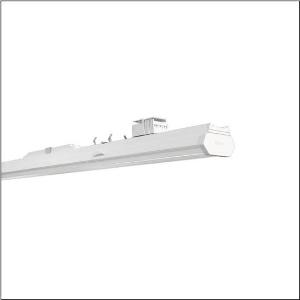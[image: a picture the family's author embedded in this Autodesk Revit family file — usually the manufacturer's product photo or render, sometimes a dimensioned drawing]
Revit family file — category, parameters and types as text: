
# Revit family: licross_r__21_protected_mo_52tp12dn4a5g_b875
name_source: partatom
category: Lighting Fixtures
units: mm (PartAtom-declared; Revit-internal decimal feet)

## family parameters
Cut with Voids When Loaded = No
Host = Face
Light Source = No
Part Type = Normal
Room Calculation Point = No
Round Connector Dimension = Use Diameter
Shared = No

## types (1)
- --- (1 x LED, 10700 lm, 62 W, 4000K)
    Apparent Load = 62 VA
    CIE Flux Codes = 73 92 98 99 100
    Color Rendering = 80
    Color Temperature = 4000K
    Default Elevation = 1800 mm
    Description = Licross® 21 Protected MO, luminaire insert, of sheet steel, galvanised, coil coated, white, length: 1.500mm, width: 90mm, height: 103mm, LED rated luminous flux: 10.700lm, light colour: 840, SDCM (Standard Deviation of Colour Matching)MacAdam ≤ 3 SDCM (initial), control gear: DALI 2, with plug, 5-pole, with phase selection, mains connection: 220..240V, AC, 50/60Hz, rated input power: 62W, internal wiring halogen-free, primary light control with lens, of plastic, primary optical cover: cover, of PMMA, light emission: direct distribution, primary light characteristic: symmetric, protection rating (complete): IP64, insulation class (complete): insulation class I (protective earthing), certification: CE, ENEC, VDE, UKCA, protection symbol: D if used in an environment with conductive dust loads with corresponding accessories, impact resistance: IK06, permissible ambient temperature for indoor applications: -25..+35°C, corresponds to IFS (International Featured Standards) requirements for safety and quality in the food industry, reducing of maximum allowable ambient temperature of 5°C with ceiling mounting, LABS conformity tested according to VDMA 24364:2018-05, packaging unit: 1 piece
    Height = 92 mm
    Lamp = 1 x LED
    Lamp Light Flux = 10700 lm
    Lamp Power = 62 W
    Lamp count = 1
    Length = 1500 mm
    Luminous efficacy = 173 lm/W
    Manufacturer = Siteco
    ModVariant = No
    Model = 52TP12DN4A5G
    Mounting Place = Ceiling
    Mounting Type = Pendant
    Number of Poles = 1
    OnlyDefault = Yes
    Power Factor = 1
    Product Name = Licross® 21 Protected MO
    Product group = luminaire insert | ceiling pendant
    ProductGroupID = 901
    Protection Class = Protection class I
    Protection Degree = IP 64
    RLX_Detail_Level = 1
    RLX_Emergency_Light_Flux = 0 lm
    RLX_Emergency_Type = 0
    RLX_Emergency_Type_DB = No
    RlxData = <blob elided: 24529 chars, md5=edf1e1ce>
    Socket = socket
    Standby Power = 0 W
    System Light Flux = 10700 lm
    System Power = 62 W
    Type Comments = factory setting: luminous flux: 100 % | dim-lin: 254 | 418 mA
    Type Image = l_1256148.jpg
    URL = http://relux.com
    VarID = @adj_132627
    Voltage = 0 V
    Weight = 0.00 kg
    Width = 88 mm

## geometry (parser evidence)
native form markers: Blend x4, Sweep x8
no freeform markers — native parametric forms only
